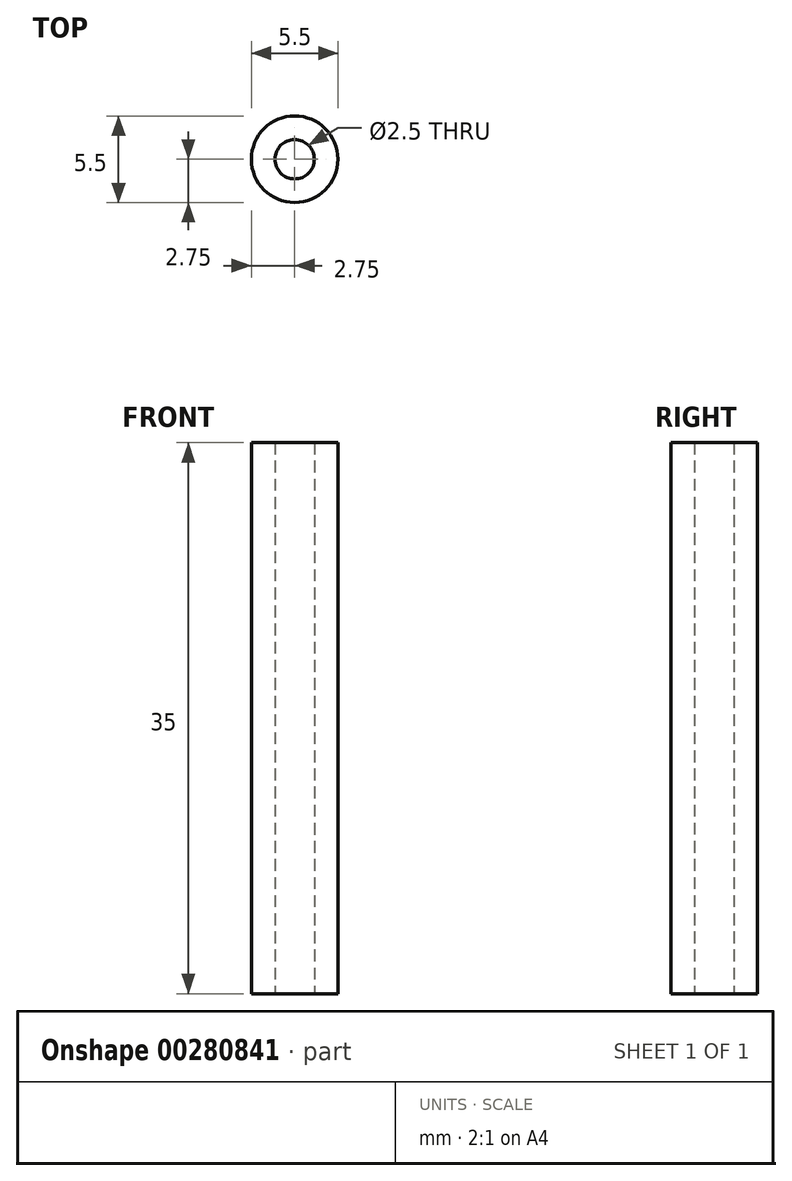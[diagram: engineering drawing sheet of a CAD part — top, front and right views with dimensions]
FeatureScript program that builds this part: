
annotation { "Feature Type Name" : "Feature", "Feature Type Description" : "" }
export const myFeature = defineFeature(function(context is Context, id is Id, definition is map)
    precondition{}
    {
        {
            var Q0;
            Q0=qCreatedBy(makeId("Top.planeOp"),FACE);
            var sketch = newSketch(context, id + "F0", { "sketchPlane" : qUnion([Q0])});
            skCircle(sketch, "E0", {"center": v(0, 0) * mm, "radius": 2.75 * mm});
            skCircle(sketch, "E1", {"center": v(0, 0) * mm, "radius": 1.25 * mm});
            skSolve(sketch);
        }
        {
            var Q0;
            Q0=makeQuery(id+"F0.imprint","IMPRINT",FACE,{"disambiguationData":[TD([[makeQuery(id+"F0.imprint","IMPRINT",EDGE,{"derivedFrom":sQuery(id+"F0.wireOp",EDGE,"E0")}),1.0]])]});
            extrude(context, id + "F1", {"entities" : qUnion([Q0]), "depth" : 35 * mm, "offsetDistance" : 25 * mm});
        }
    });
